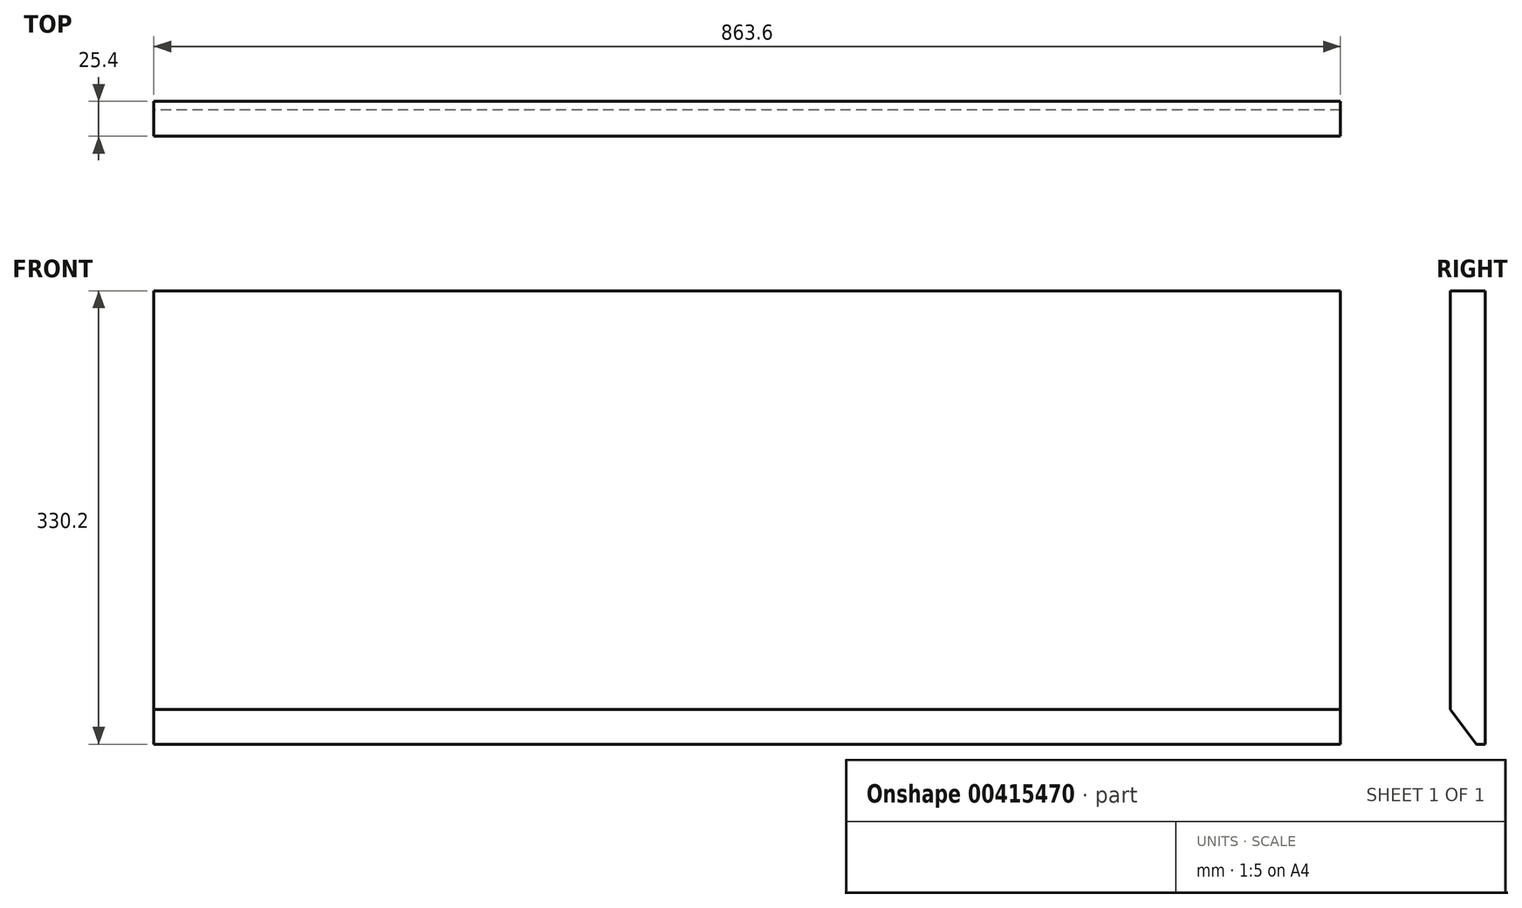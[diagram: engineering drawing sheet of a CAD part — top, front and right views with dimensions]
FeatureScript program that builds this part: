
annotation { "Feature Type Name" : "Feature", "Feature Type Description" : "" }
export const myFeature = defineFeature(function(context is Context, id is Id, definition is map)
    precondition{}
    {
        {
            var Q0;
            Q0=qCreatedBy(makeId("Front.planeOp"),FACE);
            var sketch = newSketch(context, id + "F0", { "sketchPlane" : qUnion([Q0])});
            skLineSegment(sketch, "E0.bottom", {"start": v(431.8, -165.1) * mm, "end": v(-431.8, -165.1) * mm});
            skLineSegment(sketch, "E0.top", {"start": v(431.8, 165.1) * mm, "end": v(-431.8, 165.1) * mm});
            skLineSegment(sketch, "E0.left", {"start": v(431.8, -165.1) * mm, "end": v(431.8, 165.1) * mm});
            skLineSegment(sketch, "E0.right", {"start": v(-431.8, -165.1) * mm, "end": v(-431.8, 165.1) * mm});
            skPoint(sketch, "E0.middle", {"position": v(0, 0) * mm});
            skSolve(sketch);
        }
        {
            var Q0;
            Q0=makeQuery(id+"F0.imprint","IMPRINT",FACE,{"disambiguationData":[TD([[makeQuery(id+"F0.imprint","IMPRINT",EDGE,{"derivedFrom":sQuery(id+"F0.wireOp",EDGE,"E0.bottom")}),-1.0]])]});
            extrude(context, id + "F1", {"entities" : qUnion([Q0]), "depth" : 25.4 * mm});
        }
        {
            var Q0;
            Q0=makeQuery(id+"F1.opExtrude","CAP_EDGE",EDGE,{"disambiguationData":[OSD([sQuery(id+"F0.wireOp",EDGE,"E0.bottom")])],"isStart":false});
            chamfer(context, id + "F2", {"entities" : qUnion([Q0]), "chamferType" : ChamferType.TWO_OFFSETS, "width1" : 19.05 * mm, "oppositeDirection" : false, "width2" : 25.4 * mm, "tangentPropagation" : true});
        }
    });
